# Revit family: FU_Stool_Sandler_Main-1120
name_source: partatom
category: Furniture
units: mm (PartAtom-declared; Revit-internal decimal feet)

## family parameters
Always vertical = Yes
Cut with Voids When Loaded = No
OmniClass Number = 23.40.20.00
OmniClass Title = General Furniture and Specialties
Room Calculation Point = No
Shared = No
Work Plane-Based = No

## types (1)
- FU_Stool_Sandler_Main-1120
    AC Colors = Metal - Paint - Water Blue - NCS S4050-B40G
    Default Elevation = 0 mm  [stored 0 ft]
    Depth = 450 mm  [stored 1.47638 ft]
    Description = Adjustable height stool with swivel seat in Ash wood on a steel frame
    Height = 640 mm  [stored 2.09974 ft]
    Height Adj = 640 mm  [stored 2.09974 ft]
    Manufacturer = Sandler
    Max Height = 720 mm  [stored 2.3622 ft]
    Min Height = 630 mm  [stored 2.06693 ft]
    Model = Main 1120
    URL = https://www.sandlerseating.com
    Width = 470 mm  [stored 1.54199 ft]
    Wood Seat = Wood - Beech - Chestnut Stained

note: [stored X ft] marks values corroborated as IEEE doubles in the binary element streams (Revit-internal decimal feet)

## geometry (parser evidence)
native form markers: Sweep x3
no freeform markers — native parametric forms only
